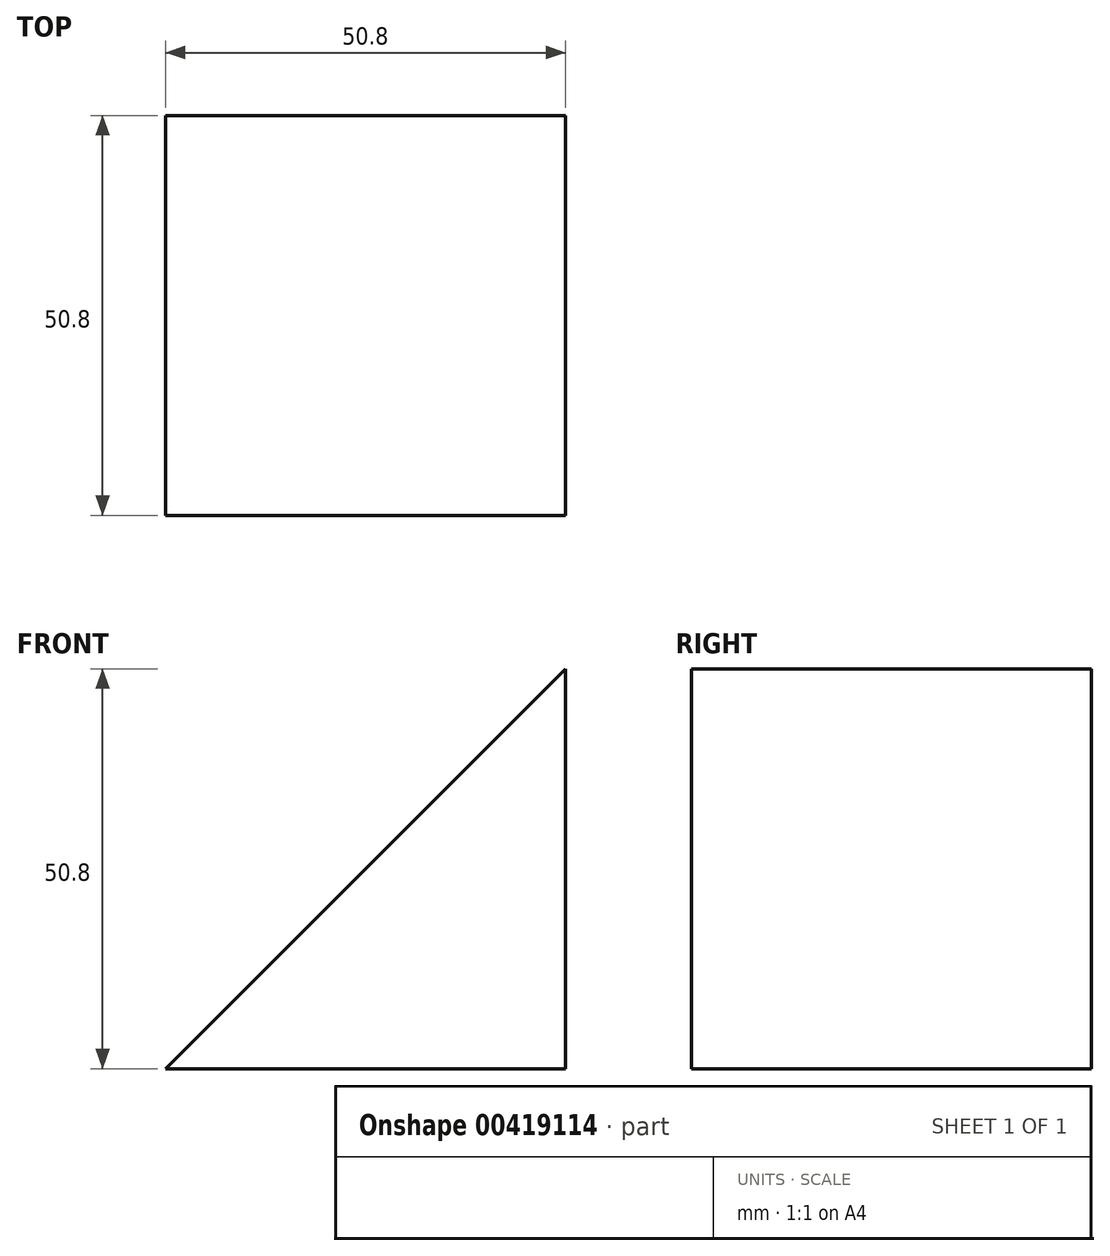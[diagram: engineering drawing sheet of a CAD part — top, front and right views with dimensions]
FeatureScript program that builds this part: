
annotation { "Feature Type Name" : "Feature", "Feature Type Description" : "" }
export const myFeature = defineFeature(function(context is Context, id is Id, definition is map)
    precondition{}
    {
        {
            var Q0;
            Q0=qCreatedBy(makeId("Front.planeOp"),FACE);
            var sketch = newSketch(context, id + "F0", { "sketchPlane" : qUnion([Q0])});
            skLineSegment(sketch, "E0", {"start": v(0, 0) * mm, "end": v(-50.8, 0) * mm});
            skLineSegment(sketch, "E1", {"start": v(0, 0) * mm, "end": v(0, 50.8) * mm});
            skLineSegment(sketch, "E2", {"start": v(-50.8, 0) * mm, "end": v(0, 50.8) * mm});
            skSolve(sketch);
        }
        {
            var Q0;
            Q0 = qSketchRegion(id + "F0", true);
            extrude(context, id + "F1", {"entities" : qUnion([Q0]), "depth" : 50.8 * mm});
        }
    });
